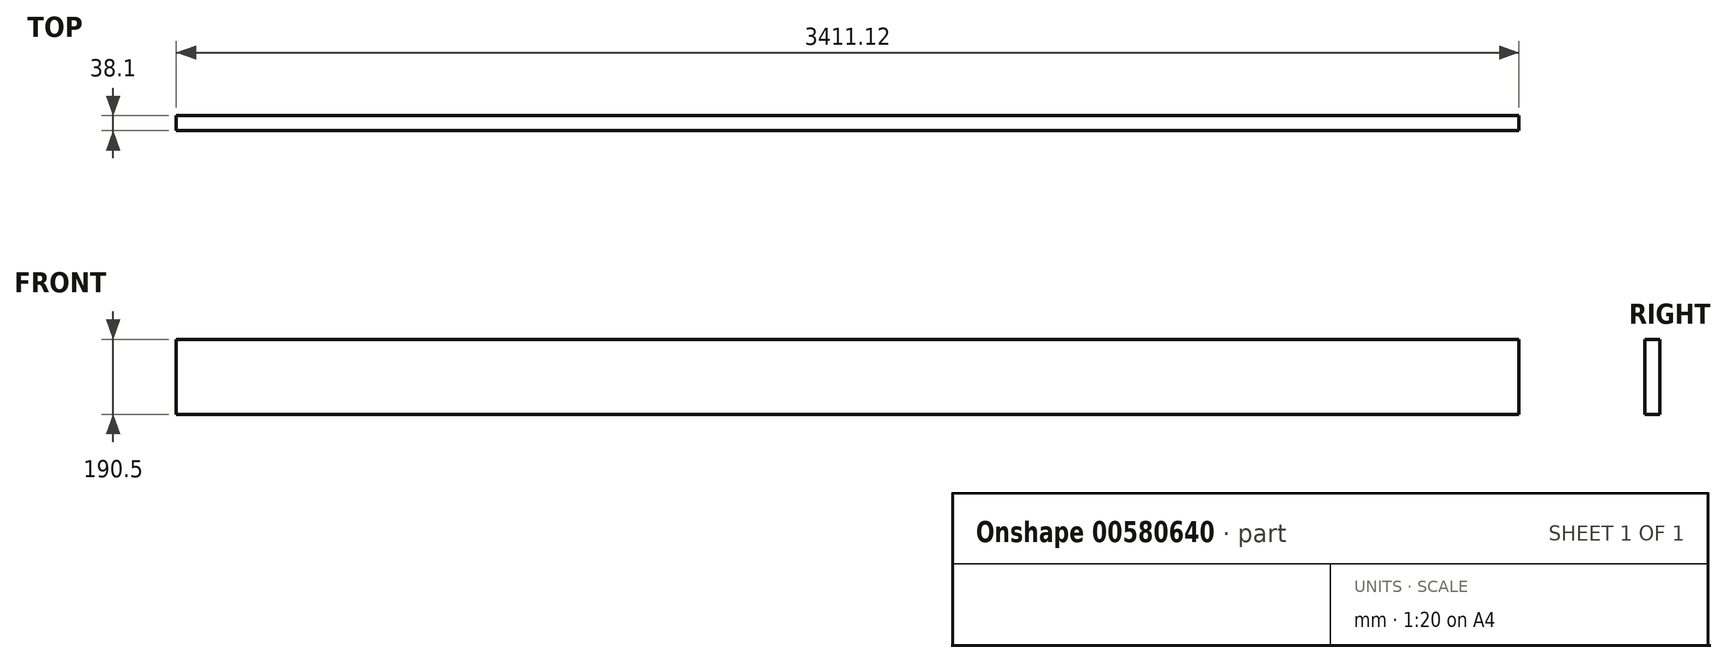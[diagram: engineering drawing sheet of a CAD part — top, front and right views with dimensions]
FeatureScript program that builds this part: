
annotation { "Feature Type Name" : "Feature", "Feature Type Description" : "" }
export const myFeature = defineFeature(function(context is Context, id is Id, definition is map)
    precondition{}
    {
        {
            var Q0;
            Q0=qCreatedBy(makeId("Top.planeOp"),FACE);
            var sketch = newSketch(context, id + "F0", { "sketchPlane" : qUnion([Q0])});
            skLineSegment(sketch, "E0.bottom", {"start": v(1705.56, -19.05) * mm, "end": v(-1705.56, -19.05) * mm});
            skLineSegment(sketch, "E0.top", {"start": v(1705.56, 19.05) * mm, "end": v(-1705.56, 19.05) * mm});
            skLineSegment(sketch, "E0.left", {"start": v(1705.56, -19.05) * mm, "end": v(1705.56, 19.05) * mm});
            skLineSegment(sketch, "E0.right", {"start": v(-1705.56, -19.05) * mm, "end": v(-1705.56, 19.05) * mm});
            skPoint(sketch, "E0.middle", {"position": v(0, 0) * mm});
            skSolve(sketch);
        }
        {
            var Q0;
            Q0=makeQuery(id+"F0.imprint","IMPRINT",FACE,{"disambiguationData":[TD([[makeQuery(id+"F0.imprint","IMPRINT",EDGE,{"derivedFrom":sQuery(id+"F0.wireOp",EDGE,"E0.bottom")}),-1.0]])]});
            extrude(context, id + "F1", {"entities" : qUnion([Q0]), "depth" : 190.5 * mm, "offsetDistance" : 25.4 * mm});
        }
    });
